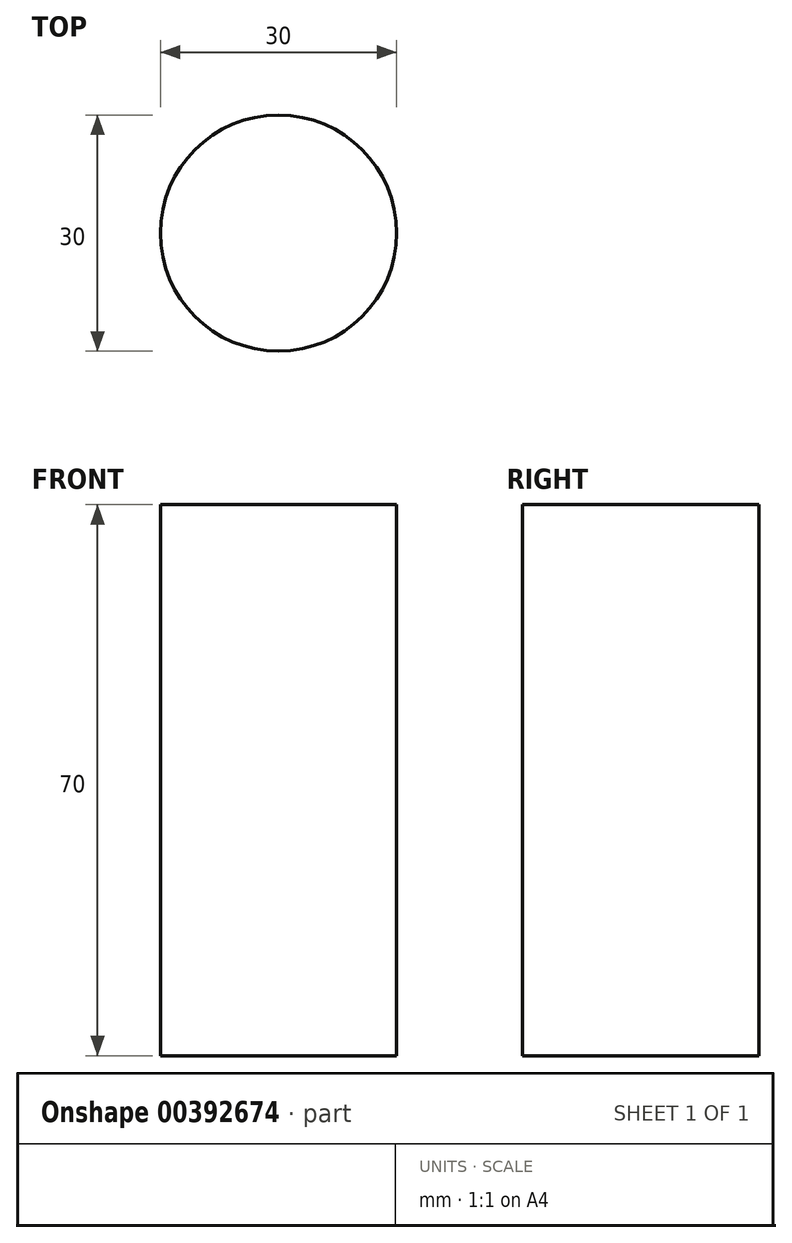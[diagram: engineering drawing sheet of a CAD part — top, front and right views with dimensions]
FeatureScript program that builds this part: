
annotation { "Feature Type Name" : "Feature", "Feature Type Description" : "" }
export const myFeature = defineFeature(function(context is Context, id is Id, definition is map)
    precondition{}
    {
        {
            var Q0;
            Q0=qCreatedBy(makeId("Top.planeOp"),FACE);
            var sketch = newSketch(context, id + "F0", { "sketchPlane" : qUnion([Q0])});
            skCircle(sketch, "E0", {"center": v(0, 0) * mm, "radius": 15 * mm});
            skSolve(sketch);
        }
        {
            var Q0;
            Q0 = qSketchRegion(id + "F0", true);
            extrude(context, id + "F1", {"entities" : qUnion([Q0]), "depth" : 70 * mm});
        }
    });
